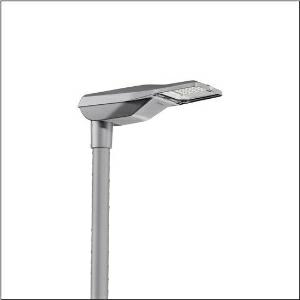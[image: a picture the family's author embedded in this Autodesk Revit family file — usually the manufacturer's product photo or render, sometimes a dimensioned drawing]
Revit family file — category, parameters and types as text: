
# Revit family: streetlight_sl_21_iq_micro___st1_0ab_5xe1m31g08cb_01f6
name_source: partatom
category: Lighting Fixtures
units: mm (PartAtom-declared; Revit-internal decimal feet)

## family parameters
Cut with Voids When Loaded = No
Host = Face
Light Source = No
Part Type = Normal
Room Calculation Point = No
Round Connector Dimension = Use Diameter
Shared = No

## types (1)
- --- (1 x LED, 2520 lm, 19.4 W, 3000K)
    Apparent Load = 19 VA
    CIE Flux Codes = 38 73 97 100 100
    Color Rendering = 70
    Color Temperature = 3000K
    Default Elevation = 1800 mm
    Description = Streetlight SL 21 iQ micro, mast luminaire, primary light control with lens, of PMMA, primary optical cover: cover, of toughened safety glass, transparent, light distribution: ST1.0aB, light emission: direct distribution, primary light characteristic: asymmetric, installation type: post-top, side-entry, LED, High Power LED, rated luminous flux: 2.520lm, luminous efficacy: 130lm/W, light colour: 730, colour temperature: 3000K, control gear: iQ Street-Remote, control: Street-Remote, Auto-Match, Temp-Guard, Lumen-Switch, Night-Set, Smart-Wire, Light-Fading, Desk-Remote (wireless, voltage-free reading and setting of iQ features in the workshop via application-optimized NFC function/RFID function), optimised constant luminous flux control (CLO 2.0), pre-setting: linear dimming characteristic, mains connection: 220..240V, AC, 50/60Hz, start of lifetime: 19W, end of service life: 20W, reduction: 10W, luminaire housing, of diecast aluminium, powder-coated, SITECO metallic grey (DB 702S), corrosivity category C5 high according to DIN EN ISO 12944, please order mast flange separately, inclination adjustable: 0°, 5°, 10°, 15°, sealing non-destructively replaceable, multi-level sealing system, length: 528mm, width: 235mm, height: 110mm, mast flange for spigot size: 42mm (side-entry): 5XC10008XM4, 60/48mm (side-entry/post-top): 5XC10108XM2, 76/60mm (side-entry/post-top): 5XC10108XM1, protection rating (complete): IP66, insulation class (complete): insulation class II (safety insulation), certification: CE, ENEC, ENEC+, VDE, impact resistance: IK10, permissible operating ambient temperature for outdoor applications: -40..+50°C, standard-compliant lighting for roads and squares, packaging unit: 1 piece

Light Distribution: ST1.0aB
    Height = 110 mm
    Lamp = 1 x LED
    Lamp Light Flux = 2520 lm
    Lamp Power = 19.4 W
    Lamp count = 1
    Length = 528 mm
    Luminous efficacy = 130 lm/W
    Manufacturer = Siteco
    ModVariant = No
    Model = 5XE1M31G08CB
    Number of Poles = 1
    OnlyDefault = Yes
    Power Factor = 1
    Product Name = Streetlight SL 21 iQ micro | ST1.0aB
    Product group = mast luminaire | pylon top
    ProductGroupID = 6100
    Protection Class = Protection class II
    Protection Degree = IP 66
    RLX_Detail_Level = 1
    RLX_Emergency_Light_Flux = 0 lm
    RLX_Emergency_Type = 0
    RLX_Emergency_Type_DB = No
    RlxData = <blob elided: 98753 chars, md5=2fba73f9>
    Socket = socket
    Standby Power = 0 W
    System Light Flux = 2520 lm
    System Power = 19 W
    Type Comments = factory setting: luminous flux: 100 % | dim-lin: 254 | 387 mA
    Type Image = l_1006881.jpg
    URL = http://relux.com
    VarID = @adj_137639
    Voltage = 0 V
    Weight = 0.00 kg
    Width = 235 mm

## geometry (parser evidence)
native form markers: Blend x4, Sweep x10
no freeform markers — native parametric forms only
